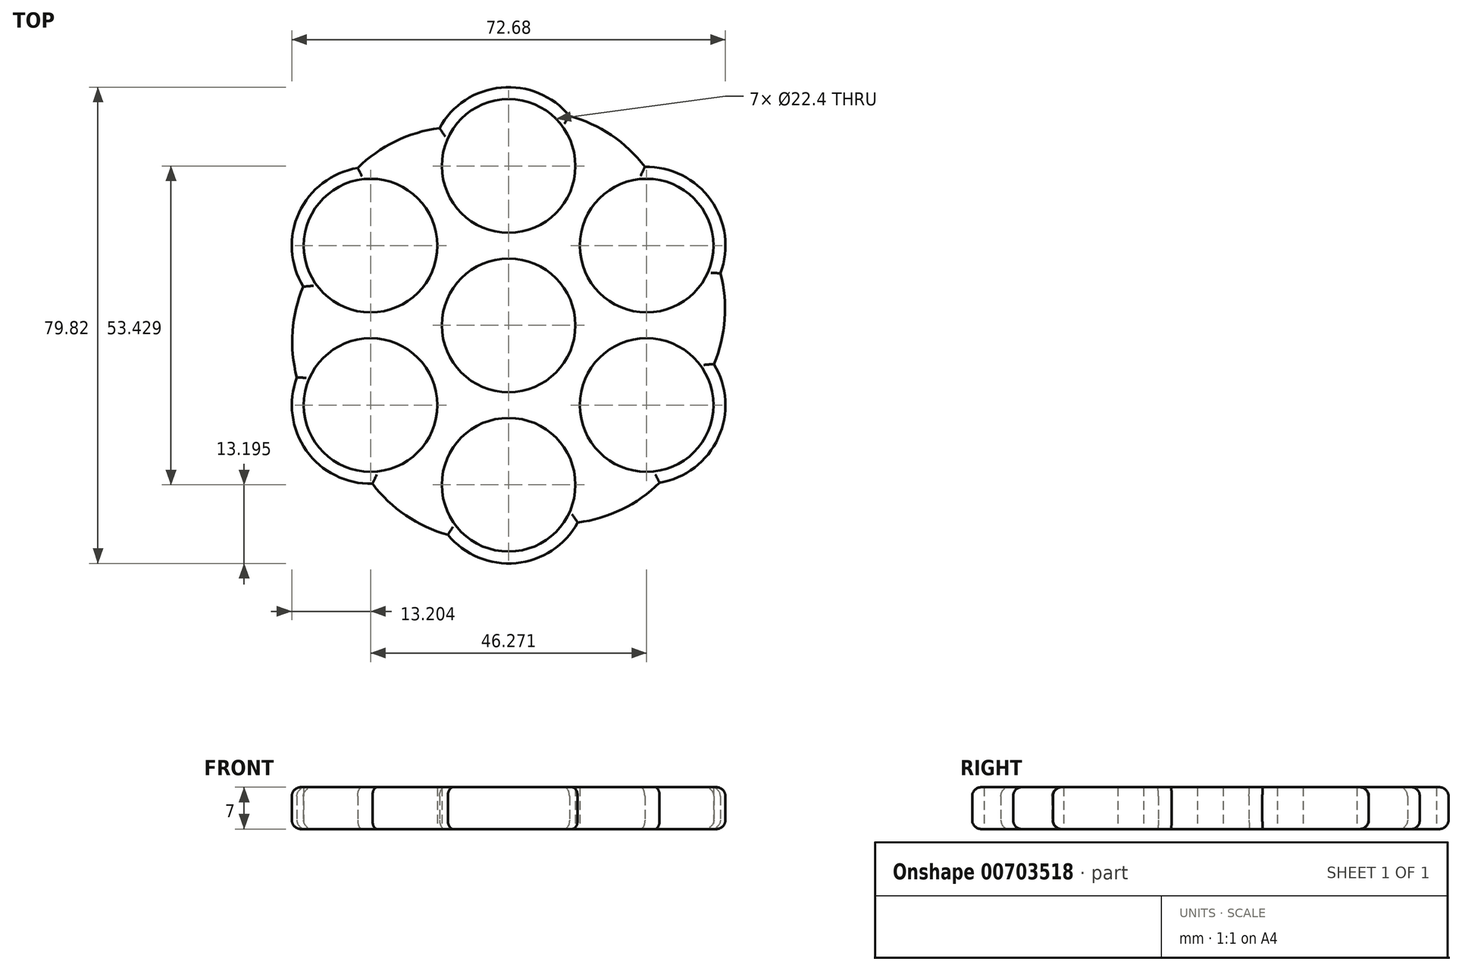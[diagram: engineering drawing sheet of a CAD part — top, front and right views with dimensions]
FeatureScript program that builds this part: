
annotation { "Feature Type Name" : "Feature", "Feature Type Description" : "" }
export const myFeature = defineFeature(function(context is Context, id is Id, definition is map)
    precondition{}
    {
        {
            var Q0;
            Q0=qCreatedBy(makeId("Top.planeOp"),FACE);
            var sketch = newSketch(context, id + "F0", { "sketchPlane" : qUnion([Q0])});
            skCircle(sketch, "E0", {"center": v(0, 0) * mm, "radius": 11.2 * mm});
            skCircle(sketch, "E1", {"center": v(0, 26.71) * mm, "radius": 11.2 * mm});
            skArc(sketch, "E2", {"start": v(10.2, 35.1) * mm, "mid": v(-1.24, 39.86) * mm, "end": v(-11.58, 33.05) * mm});
            skArc(sketch, "E3.1.0", {"start": v(-25.3, 26.38) * mm, "mid": v(-35.14, 18.85) * mm, "end": v(-34.4, 6.5) * mm});
            skCircle(sketch, "E3.1.1", {"center": v(-23.14, 13.36) * mm, "radius": 11.2 * mm});
            skArc(sketch, "E3.2.0", {"start": v(-35.5, -8.72) * mm, "mid": v(-33.9, -21) * mm, "end": v(-22.83, -26.55) * mm});
            skCircle(sketch, "E3.2.1", {"center": v(-23.14, -13.36) * mm, "radius": 11.2 * mm});
            skArc(sketch, "E3.3.0", {"start": v(-10.2, -35.1) * mm, "mid": v(1.24, -39.86) * mm, "end": v(11.58, -33.05) * mm});
            skCircle(sketch, "E3.3.1", {"center": v(0, -26.71) * mm, "radius": 11.2 * mm});
            skArc(sketch, "E3.4.0", {"start": v(25.3, -26.38) * mm, "mid": v(35.14, -18.85) * mm, "end": v(34.4, -6.5) * mm});
            skCircle(sketch, "E3.4.1", {"center": v(23.14, -13.36) * mm, "radius": 11.2 * mm});
            skArc(sketch, "E3.5.0", {"start": v(35.5, 8.72) * mm, "mid": v(33.9, 21) * mm, "end": v(22.83, 26.55) * mm});
            skCircle(sketch, "E3.5.1", {"center": v(23.14, 13.36) * mm, "radius": 11.2 * mm});
            skArc(sketch, "E4", {"start": v(-11.58, 33.05) * mm, "mid": v(-19, 30.84) * mm, "end": v(-25.3, 26.38) * mm});
            skArc(sketch, "E5.1.0", {"start": v(-34.4, 6.5) * mm, "mid": v(-36.2, -1.03) * mm, "end": v(-35.5, -8.72) * mm});
            skArc(sketch, "E5.2.0", {"start": v(-22.83, -26.55) * mm, "mid": v(-17.22, -31.87) * mm, "end": v(-10.2, -35.1) * mm});
            skArc(sketch, "E5.3.0", {"start": v(11.58, -33.05) * mm, "mid": v(19, -30.84) * mm, "end": v(25.3, -26.38) * mm});
            skArc(sketch, "E5.4.0", {"start": v(34.4, -6.5) * mm, "mid": v(36.2, 1.03) * mm, "end": v(35.5, 8.72) * mm});
            skArc(sketch, "E5.5.0", {"start": v(22.83, 26.55) * mm, "mid": v(17.22, 31.87) * mm, "end": v(10.2, 35.1) * mm});
            skSolve(sketch);
        }
        {
            var Q0;
            Q0=makeQuery(id+"F0.imprint","IMPRINT",FACE,{"disambiguationData":[TD([[makeQuery(id+"F0.imprint","IMPRINT",EDGE,{"derivedFrom":sQuery(id+"F0.wireOp",EDGE,"E0")}),-1.0]])]});
            extrude(context, id + "F1", {"entities" : qUnion([Q0]), "depth" : 7 * mm, "offsetDistance" : 25 * mm});
        }
        {
            var Q0;
            Q0=makeQuery(id+"F1.opExtrude","CAP_EDGE",EDGE,{"disambiguationData":[OSD([sQuery(id+"F0.wireOp",EDGE,"E5.2.0")])],"isStart":true});
            var Q1;
            Q1=makeQuery(id+"F1.opExtrude","CAP_EDGE",EDGE,{"disambiguationData":[OSD([sQuery(id+"F0.wireOp",EDGE,"E3.3.0")])],"isStart":true});
            var Q2;
            Q2=makeQuery(id+"F1.opExtrude","CAP_EDGE",EDGE,{"disambiguationData":[OSD([sQuery(id+"F0.wireOp",EDGE,"E5.3.0")])],"isStart":true});
            var Q3;
            Q3=makeQuery(id+"F1.opExtrude","CAP_EDGE",EDGE,{"disambiguationData":[OSD([sQuery(id+"F0.wireOp",EDGE,"E3.4.0")])],"isStart":true});
            var Q4;
            Q4=makeQuery(id+"F1.opExtrude","CAP_EDGE",EDGE,{"disambiguationData":[OSD([sQuery(id+"F0.wireOp",EDGE,"E5.4.0")])],"isStart":true});
            var Q5;
            Q5=makeQuery(id+"F1.opExtrude","CAP_EDGE",EDGE,{"disambiguationData":[OSD([sQuery(id+"F0.wireOp",EDGE,"E3.5.0")])],"isStart":true});
            var Q6;
            Q6=makeQuery(id+"F1.opExtrude","CAP_EDGE",EDGE,{"disambiguationData":[OSD([sQuery(id+"F0.wireOp",EDGE,"E5.5.0")])],"isStart":true});
            var Q7;
            Q7=makeQuery(id+"F1.opExtrude","CAP_EDGE",EDGE,{"disambiguationData":[OSD([sQuery(id+"F0.wireOp",EDGE,"E2")])],"isStart":true});
            var Q8;
            Q8=makeQuery(id+"F1.opExtrude","CAP_EDGE",EDGE,{"disambiguationData":[OSD([sQuery(id+"F0.wireOp",EDGE,"E4")])],"isStart":true});
            var Q9;
            Q9=makeQuery(id+"F1.opExtrude","CAP_EDGE",EDGE,{"disambiguationData":[OSD([sQuery(id+"F0.wireOp",EDGE,"E3.1.0")])],"isStart":true});
            var Q10;
            Q10=makeQuery(id+"F1.opExtrude","CAP_EDGE",EDGE,{"disambiguationData":[OSD([sQuery(id+"F0.wireOp",EDGE,"E5.1.0")])],"isStart":true});
            var Q11;
            Q11=makeQuery(id+"F1.opExtrude","CAP_EDGE",EDGE,{"disambiguationData":[OSD([sQuery(id+"F0.wireOp",EDGE,"E3.2.0")])],"isStart":true});
            fillet(context, id + "F2", {"entities" : qUnion([Q0, Q1, Q2, Q3, Q4, Q5, Q6, Q7, Q8, Q9, Q10, Q11]), "radius" : 1.5 * mm, "tangentPropagation" : true, "allowEdgeOverflow" : false});
        }
        {
            var Q0;
            Q0=makeQuery(id+"F1.opExtrude","CAP_EDGE",EDGE,{"disambiguationData":[OSD([sQuery(id+"F0.wireOp",EDGE,"E4")])],"isStart":false});
            var Q1;
            Q1=makeQuery(id+"F1.opExtrude","CAP_EDGE",EDGE,{"disambiguationData":[OSD([sQuery(id+"F0.wireOp",EDGE,"E2")])],"isStart":false});
            var Q2;
            Q2=makeQuery(id+"F1.opExtrude","CAP_EDGE",EDGE,{"disambiguationData":[OSD([sQuery(id+"F0.wireOp",EDGE,"E5.5.0")])],"isStart":false});
            var Q3;
            Q3=makeQuery(id+"F1.opExtrude","CAP_EDGE",EDGE,{"disambiguationData":[OSD([sQuery(id+"F0.wireOp",EDGE,"E3.5.0")])],"isStart":false});
            var Q4;
            Q4=makeQuery(id+"F1.opExtrude","CAP_EDGE",EDGE,{"disambiguationData":[OSD([sQuery(id+"F0.wireOp",EDGE,"E5.4.0")])],"isStart":false});
            var Q5;
            Q5=makeQuery(id+"F1.opExtrude","CAP_EDGE",EDGE,{"disambiguationData":[OSD([sQuery(id+"F0.wireOp",EDGE,"E3.4.0")])],"isStart":false});
            var Q6;
            Q6=makeQuery(id+"F1.opExtrude","CAP_EDGE",EDGE,{"disambiguationData":[OSD([sQuery(id+"F0.wireOp",EDGE,"E5.3.0")])],"isStart":false});
            var Q7;
            Q7=makeQuery(id+"F1.opExtrude","CAP_EDGE",EDGE,{"disambiguationData":[OSD([sQuery(id+"F0.wireOp",EDGE,"E3.3.0")])],"isStart":false});
            var Q8;
            Q8=makeQuery(id+"F1.opExtrude","CAP_EDGE",EDGE,{"disambiguationData":[OSD([sQuery(id+"F0.wireOp",EDGE,"E5.2.0")])],"isStart":false});
            var Q9;
            Q9=makeQuery(id+"F1.opExtrude","CAP_EDGE",EDGE,{"disambiguationData":[OSD([sQuery(id+"F0.wireOp",EDGE,"E3.2.0")])],"isStart":false});
            var Q10;
            Q10=makeQuery(id+"F1.opExtrude","CAP_EDGE",EDGE,{"disambiguationData":[OSD([sQuery(id+"F0.wireOp",EDGE,"E5.1.0")])],"isStart":false});
            var Q11;
            Q11=makeQuery(id+"F1.opExtrude","CAP_EDGE",EDGE,{"disambiguationData":[OSD([sQuery(id+"F0.wireOp",EDGE,"E3.1.0")])],"isStart":false});
            fillet(context, id + "F3", {"entities" : qUnion([Q0, Q1, Q2, Q3, Q4, Q5, Q6, Q7, Q8, Q9, Q10, Q11]), "radius" : 1.5 * mm, "tangentPropagation" : true, "allowEdgeOverflow" : false});
        }
    });
